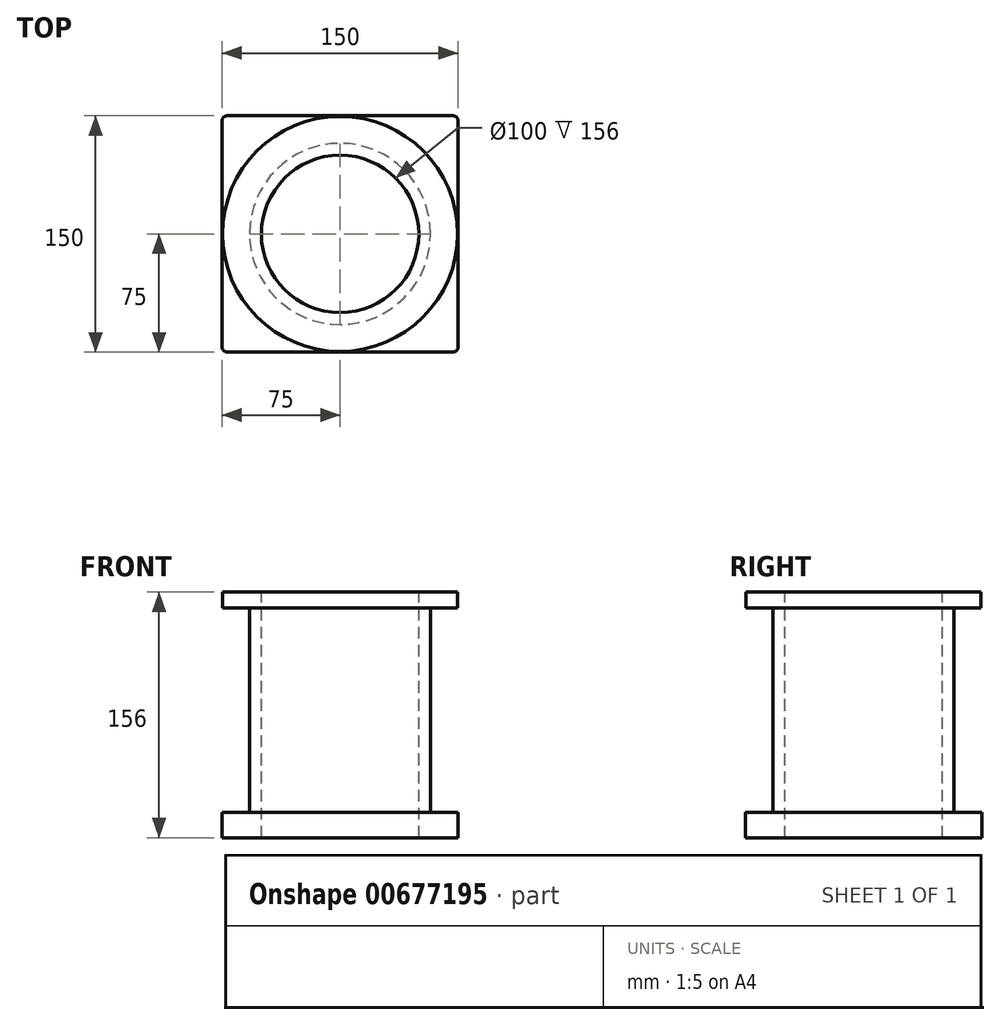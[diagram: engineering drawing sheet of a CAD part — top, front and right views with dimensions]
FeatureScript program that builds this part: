
annotation { "Feature Type Name" : "Feature", "Feature Type Description" : "" }
export const myFeature = defineFeature(function(context is Context, id is Id, definition is map)
    precondition{}
    {
        {
            var Q0;
            Q0=qCreatedBy(makeId("Top.planeOp"),FACE);
            var sketch = newSketch(context, id + "F0", { "sketchPlane" : qUnion([Q0])});
            skLineSegment(sketch, "E0.bottom", {"start": v(75, -75) * mm, "end": v(-75, -75) * mm});
            skLineSegment(sketch, "E0.top", {"start": v(75, 75) * mm, "end": v(-75, 75) * mm});
            skLineSegment(sketch, "E0.left", {"start": v(75, -75) * mm, "end": v(75, 75) * mm});
            skLineSegment(sketch, "E0.right", {"start": v(-75, -75) * mm, "end": v(-75, 75) * mm});
            skPoint(sketch, "E0.middle", {"position": v(0, 0) * mm});
            skSolve(sketch);
        }
        {
            var Q0;
            Q0 = qSketchRegion(id + "F0", true);
            extrude(context, id + "F1", {"entities" : qUnion([Q0]), "depth" : 16 * mm, "offsetDistance" : 25 * mm});
        }
        {
            var Q0;
            Q0=makeQuery(id+"F1.opExtrude","SWEPT_EDGE",EDGE,{"disambiguationData":[OSD([sQuery(id+"F0.wireOp",EDGE,"E0.top"),sQuery(id+"F0.wireOp",EDGE,"E0.right")])]});
            var Q1;
            Q1=makeQuery(id+"F1.opExtrude","SWEPT_EDGE",EDGE,{"disambiguationData":[OSD([sQuery(id+"F0.wireOp",EDGE,"E0.top"),sQuery(id+"F0.wireOp",EDGE,"E0.left")])]});
            var Q2;
            Q2=makeQuery(id+"F1.opExtrude","SWEPT_EDGE",EDGE,{"disambiguationData":[OSD([sQuery(id+"F0.wireOp",EDGE,"E0.bottom"),sQuery(id+"F0.wireOp",EDGE,"E0.left")])]});
            var Q3;
            Q3=makeQuery(id+"F1.opExtrude","SWEPT_EDGE",EDGE,{"disambiguationData":[OSD([sQuery(id+"F0.wireOp",EDGE,"E0.bottom"),sQuery(id+"F0.wireOp",EDGE,"E0.right")])]});
            fillet(context, id + "F2", {"entities" : qUnion([Q0, Q1, Q2, Q3]), "radius" : 3.2 * mm, "tangentPropagation" : true, "allowEdgeOverflow" : false});
        }
        {
            var Q0;
            Q0=makeQuery(id+"F1.opExtrude","CAP_FACE",FACE,{"disambiguationData":[OSD([sQuery(id+"F0.wireOp",EDGE,"E0.bottom"),sQuery(id+"F0.wireOp",EDGE,"E0.top"),sQuery(id+"F0.wireOp",EDGE,"E0.left"),sQuery(id+"F0.wireOp",EDGE,"E0.right")])],"isStart":false});
            var sketch = newSketch(context, id + "F3", { "sketchPlane" : qUnion([Q0])});
            skSolve(sketch);
        }
        {
            var Q0;
            {var subQ3=sQuery(id+"F0.wireOp",EDGE,"E0.bottom");Q0=makeQuery(id+"F3.imprint","IMPRINT",FACE,{"disambiguationData":[TD([[makeQuery(id+"F3.imprint","IMPRINT",EDGE,{"derivedFrom":makeQuery(id+"F1.opExtrude","CAP_EDGE",EDGE,{"disambiguationData":[OSD([subQ3])],"isStart":false})}),-1.0]])]});}
            var sketch = newSketch(context, id + "F4", { "sketchPlane" : qUnion([Q0])});
            skCircle(sketch, "E1", {"center": v(0, 0) * mm, "radius": 57.5 * mm});
            skSolve(sketch);
        }
        {
            var Q0;
            Q0 = qSketchRegion(id + "F4", true);
            extrude(context, id + "F5", {"entities" : qUnion([Q0]), "operationType" : NewBodyOperationType.ADD, "depth" : 130 * mm, "offsetDistance" : 25 * mm});
        }
        {
            var Q0;
            Q0=makeQuery(id+"F5.opExtrude","CAP_FACE",FACE,{"disambiguationData":[OSD([sQuery(id+"F4.wireOp",EDGE,"E1")])],"isStart":false});
            var sketch = newSketch(context, id + "F6", { "sketchPlane" : qUnion([Q0])});
            skCircle(sketch, "E2", {"center": v(0, 0) * mm, "radius": 50 * mm});
            skSolve(sketch);
        }
        {
            var Q0;
            Q0 = qSketchRegion(id + "F6", true);
            extrude(context, id + "F7", {"entities" : qUnion([Q0]), "operationType" : NewBodyOperationType.REMOVE, "endBound" : BoundingType.THROUGH_ALL, "oppositeDirection" : true, "depth" : 25 * mm, "offsetDistance" : 25 * mm});
        }
        {
            var Q0;
            Q0=makeQuery(id+"F5.opExtrude","CAP_FACE",FACE,{"disambiguationData":[OSD([sQuery(id+"F4.wireOp",EDGE,"E1")])],"isStart":false});
            var sketch = newSketch(context, id + "F8", { "sketchPlane" : qUnion([Q0])});
            skCircle(sketch, "E3", {"center": v(0, 0) * mm, "radius": 74.63 * mm});
            skSolve(sketch);
        }
        {
            var Q0;
            Q0=makeQuery(id+"F8.imprint","IMPRINT",FACE,{"disambiguationData":[TD([[makeQuery(id+"F8.imprint","IMPRINT",EDGE,{"derivedFrom":sQuery(id+"F8.wireOp",EDGE,"E3")}),1.0]])]});
            var sketch = newSketch(context, id + "F9", { "sketchPlane" : qUnion([Q0])});
            skCircle(sketch, "E4.0", {"center": v(0, 0) * mm, "radius": 74.63 * mm});
            skCircle(sketch, "E5.0", {"center": v(0, 0) * mm, "radius": 50 * mm});
            skSolve(sketch);
        }
        {
            var Q0;
            Q0 = qSketchRegion(id + "F9", true);
            extrude(context, id + "F10", {"entities" : qUnion([Q0]), "operationType" : NewBodyOperationType.ADD, "depth" : 10 * mm, "offsetDistance" : 25 * mm});
        }
    });
